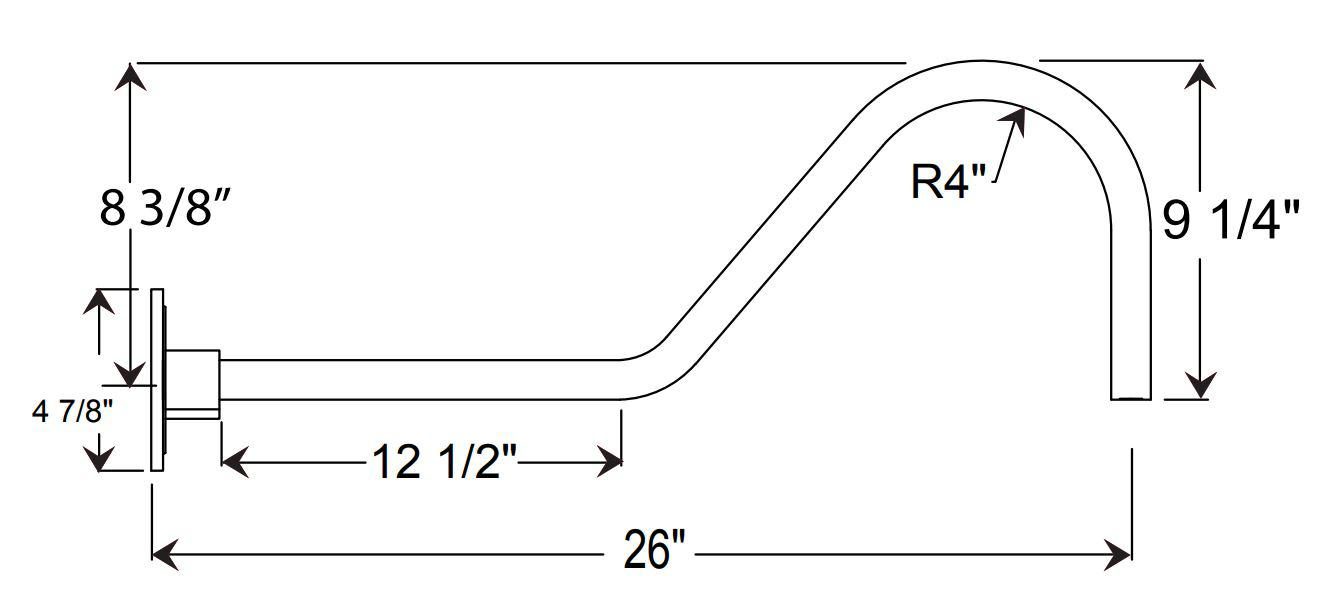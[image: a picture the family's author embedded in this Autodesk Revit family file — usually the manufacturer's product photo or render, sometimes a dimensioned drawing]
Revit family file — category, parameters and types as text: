
# Revit family: Parabowl 08,10 LED
name_source: partatom
category: Lighting Fixtures
units: mm (PartAtom-declared; Revit-internal decimal feet)

## family parameters
Always vertical = Yes
Cut with Voids When Loaded = No
Light Source = Yes
OmniClass Number = 23.80.70.00
OmniClass Title = Lighting
Part Type = Normal
Room Calculation Point = No
Round Connector Dimension = Use Diameter
Shared = No
Work Plane-Based = No

## types (2) — shared parameters
Apparent Load = 16 VA
Body Colour = Spun aluminium
Body Material = body
Bulb = BULB
CRI = >90
Canopy Body = body
Color Filter = 16777215
Construction Material = Heavy Duty spun aluminum.
Default Elevation = 0' - 0"
Description = 120-277 Voltage
Dimming = 1%
Dimming Lamp Color Temperature Shift = <None>
Efficiency = 97-125 lumens per watt
INSIDE BODY = Default
Lamp = LED
Life = L70 50,000 hours
Load Classification = Lighting
Manufacturer = ANP Lighting
Photometric Web File = generic.ies
Power Factor = 1
Tilt Angle = 90.00°
URL = https://www.anplighting.com
Voltage = 277 V
Warranty = 5 year limited warranty
Wattage Comments = 16 W
b = 0' - 2"

## per-type parameters (varying)
| type | Fixture Diameter | Fixture Height | PB08 | PB10 | Weight | a |
| PB08 | 0' - 8" | 1' - 3 3/4" | Yes | No | 2.5 lbs | 0' - 11" |
| PB10 | 0' - 10" | 1' - 7 3/4" | No | Yes | 4.0 lbs | 1' - 1" |

note: column(s) folded — value = type name in every type: Model

## geometry (parser evidence)
native form markers: Sweep x26
no freeform markers — native parametric forms only
